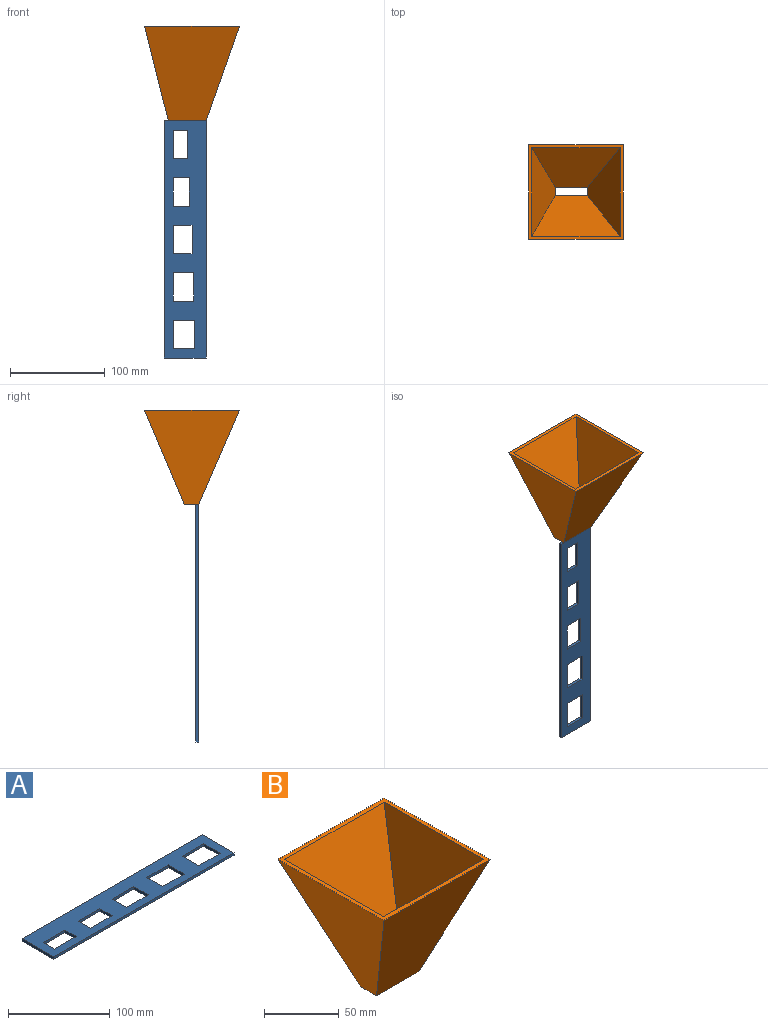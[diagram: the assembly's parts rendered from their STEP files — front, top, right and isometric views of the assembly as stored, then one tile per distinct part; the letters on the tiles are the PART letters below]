
ASSEMBLY  parts=2 mates=1
PART A: 26 faces, bbox 250x44x3 mm
  f0: plane 30x3mm, normal (0,1,0), area 90mm2, adj f1,f23,f24,f25
  f1: plane 15.5x3mm, normal (1,0,0), area 46.5mm2, adj f0,f2,f24,f25
  f2: plane 30x3mm, normal (0,-1,0), area 90mm2, adj f1,f23,f24,f25
  f3: plane 30x3mm, normal (0,1,0), area 90mm2, adj f4,f18,f24,f25
  f4: plane 20x3mm, normal (1,0,0), area 60mm2, adj f3,f5,f24,f25
  f5: plane 30x3mm, normal (0,-1,0), area 90mm2, adj f4,f18,f24,f25
  f6: plane 30x3mm, normal (0,1,0), area 90mm2, adj f7,f19,f24,f25
  f7: plane 22x3mm, normal (1,0,0), area 66mm2, adj f6,f8,f24,f25
  f8: plane 30x3mm, normal (0,-1,0), area 90mm2, adj f7,f19,f24,f25
  f9: plane 30x3mm, normal (0,1,0), area 90mm2, adj f10,f20,f24,f25
  f10: plane 23x3mm, normal (1,0,0), area 69mm2, adj f9,f11,f24,f25
  f11: plane 30x3mm, normal (0,-1,0), area 90mm2, adj f10,f20,f24,f25
  f12: plane 30x3mm, normal (0,1,0), area 90mm2, adj f13,f21,f24,f25
  f13: plane 17x3mm, normal (1,0,0), area 51mm2, adj f12,f14,f24,f25
  f14: plane 30x3mm, normal (0,-1,0), area 90mm2, adj f13,f21,f24,f25
  f15: plane 44x3mm, normal (-1,0,0), area 132mm2, adj f16,f22,f24,f25
  f16: plane 250x3mm, normal (0,-1,0), area 750mm2, adj f15,f17,f24,f25
  f17: plane 44x3mm, normal (1,0,0), area 132mm2, adj f16,f22,f24,f25
  f18: plane 20x3mm, normal (-1,0,0), area 60mm2, adj f3,f5,f24,f25
  f19: plane 22x3mm, normal (-1,0,0), area 66mm2, adj f6,f8,f24,f25
  f20: plane 23x3mm, normal (-1,0,0), area 69mm2, adj f9,f11,f24,f25
  f21: plane 17x3mm, normal (-1,0,0), area 51mm2, adj f12,f14,f24,f25
  f22: plane 250x3mm, normal (0,1,0), area 750mm2, adj f15,f17,f24,f25
  f23: plane 15.5x3mm, normal (-1,0,0), area 46.5mm2, adj f0,f2,f24,f25
  f24: plane 250x44mm, normal (0,0,1), area 8075mm2, adj f0,f1,f2,f3,f4,f5,f6,f7
  f25: plane 250x44mm, normal (0,0,-1), area 8075mm2, adj f0,f1,f2,f3,f4,f5,f6,f7
PART B: 10 faces, bbox 100x100x100 mm
  f0: plane 100x100mm, normal (0,0,1), area 1238.1mm2, adj f2,f3,f4,f5,f6,f7,f8,f9
  f1: plane 40x15mm, normal (0,0,-1), area 314mm2, adj f2,f3,f4,f5,f6,f7,f8,f9
  f2: plane 100x100mm, normal (0,0.92,-0.4), area 7619.7mm2, adj f0,f1,f3,f5
  f3: plane 100x100mm, normal (0.97,0,-0.24), area 5927mm2, adj f0,f1,f2,f4
  f4: plane 100x100mm, normal (0,-0.92,-0.39), area 7592.3mm2, adj f0,f1,f3,f5
  f5: plane 100x100mm, normal (-0.94,0,-0.33), area 6092mm2, adj f0,f1,f2,f4
  f6: plane 100x93.73mm, normal (0,-0.92,0.4), area 6937.1mm2, adj f0,f1,f7,f9
  f7: plane 100x93.48mm, normal (-0.97,0,0.24), area 5255mm2, adj f0,f1,f6,f8
  f8: plane 100x93.73mm, normal (0,0.92,0.39), area 6912.2mm2, adj f0,f1,f7,f9
  f9: plane 100x93.48mm, normal (0.94,0,0.33), area 5401.3mm2, adj f0,f1,f6,f8
PLACE A rot(axis=(0.58,0.58,-0.58),120deg) t=(-26.72,132.47,-64.87)mm
PLACE B rot(axis=(0,0,1),180deg) t=(52.28,86.47,-64.87)mm fixed
MATE planar B.f1 <-> A.f15  axis (0,0,-1) through (-19.63,141.22,-64.87)mm
